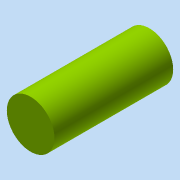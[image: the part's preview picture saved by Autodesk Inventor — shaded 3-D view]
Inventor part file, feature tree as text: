
AUTODESK INVENTOR PART (.ipt)
format: ipt  version: 2015 (Build 190159000, 159)  size: 81,408 bytes
history: native  units: in
note: dims shown in document units (in); Inventor stores cm internally (conversion verified against a paired STEP export)
features: extrude x1, sketch x1
ambient origin geometry x8: Origin, YZ Plane, XZ Plane, XY Plane, X Axis, Y Axis, Z Axis, Center Point
bodies: Solid1 (feature_tree)
feature tree (2):
  extrude  "Extrusion1"  Depth=2.565in TaperAngle=0.0deg
  sketch  "Sketch1"  dims[d0=1.0295in d1=2.565in d2=0.0in]
